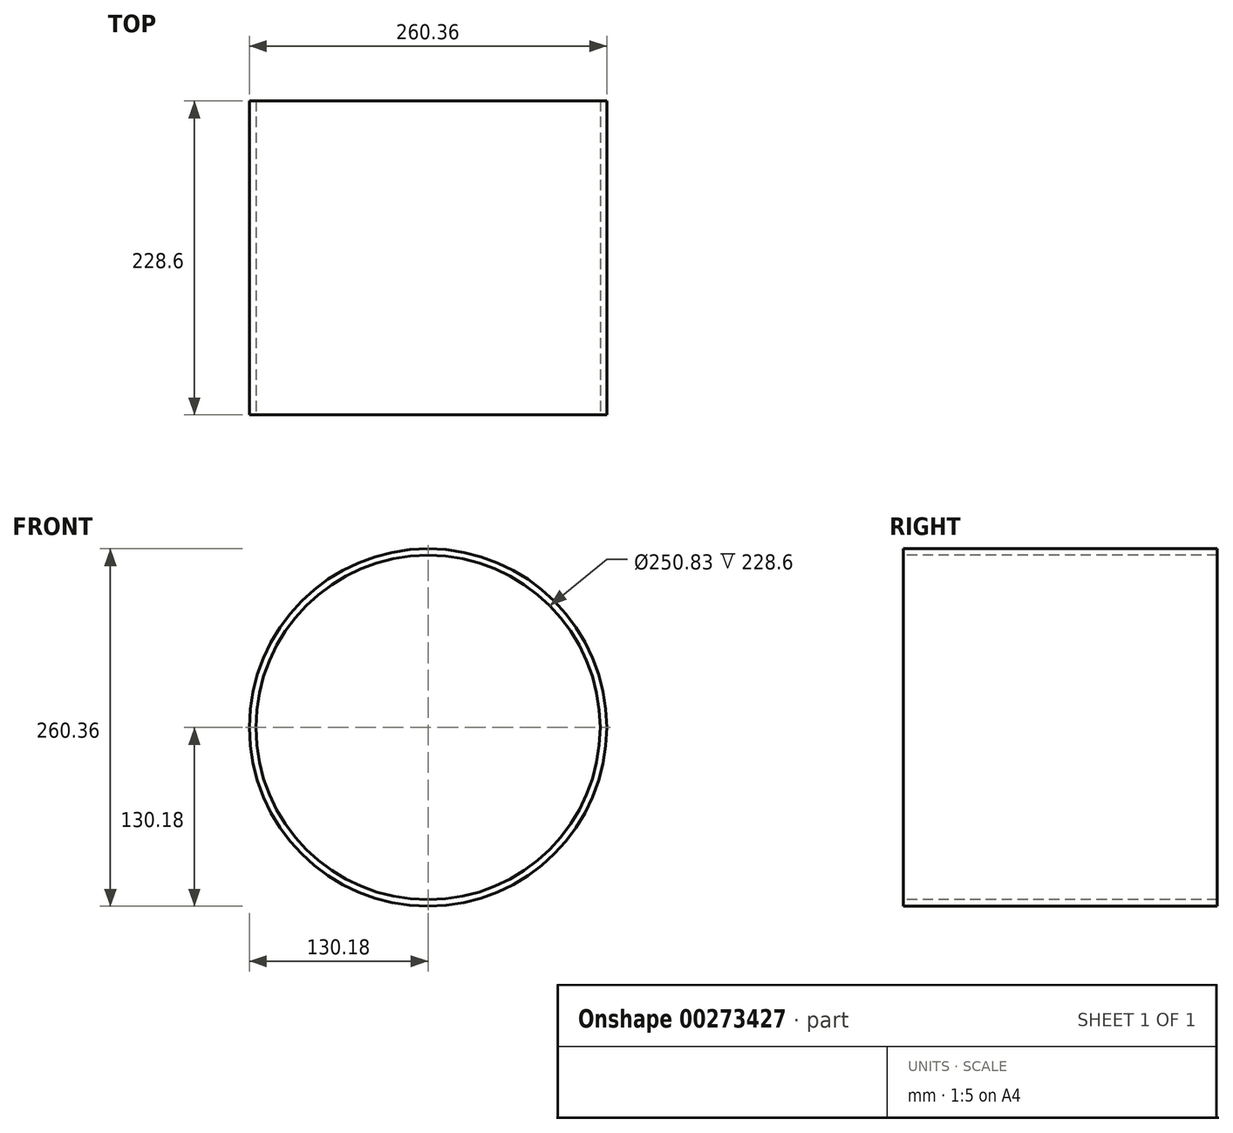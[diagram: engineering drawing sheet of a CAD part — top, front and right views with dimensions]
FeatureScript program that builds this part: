
annotation { "Feature Type Name" : "Feature", "Feature Type Description" : "" }
export const myFeature = defineFeature(function(context is Context, id is Id, definition is map)
    precondition{}
    {
        {
            var Q0;
            Q0=qCreatedBy(makeId("Right.planeOp"),FACE);
            var sketch = newSketch(context, id + "F0", { "sketchPlane" : qUnion([Q0])});
            skLineSegment(sketch, "E0", {"start": v(-23.86, 0) * mm, "end": v(28, 0) * mm, "construction": true});
            skSolve(sketch);
        }
        {
            var Q0;
            Q0=qCreatedBy(makeId("Right.planeOp"),FACE);
            var sketch = newSketch(context, id + "F1", { "sketchPlane" : qUnion([Q0])});
            skLineSegment(sketch, "E1", {"start": v(-114.3, -125.41) * mm, "end": v(114.3, -125.41) * mm});
            skLineSegment(sketch, "E2.0", {"start": v(-114.3, -130.18) * mm, "end": v(114.3, -130.17) * mm});
            skLineSegment(sketch, "E3", {"start": v(-114.3, -125.41) * mm, "end": v(-114.3, -130.18) * mm});
            skLineSegment(sketch, "E4", {"start": v(114.3, -125.41) * mm, "end": v(114.3, -130.17) * mm});
            skSolve(sketch);
        }
        {
            var Q0;
            Q0=makeQuery(id+"F1.imprint","IMPRINT",FACE,{"disambiguationData":[TD([[makeQuery(id+"F1.imprint","IMPRINT",EDGE,{"derivedFrom":sQuery(id+"F1.wireOp",EDGE,"E1")}),-1.0]])]});
            var Q1;
            Q1=sQuery(id+"F0.wireOp",EDGE,"E0");
            revolve(context, id + "F2", {"entities" : qUnion([Q0]), "axis" : qUnion([Q1]), "revolveType" : RevolveType.FULL});
        }
    });
